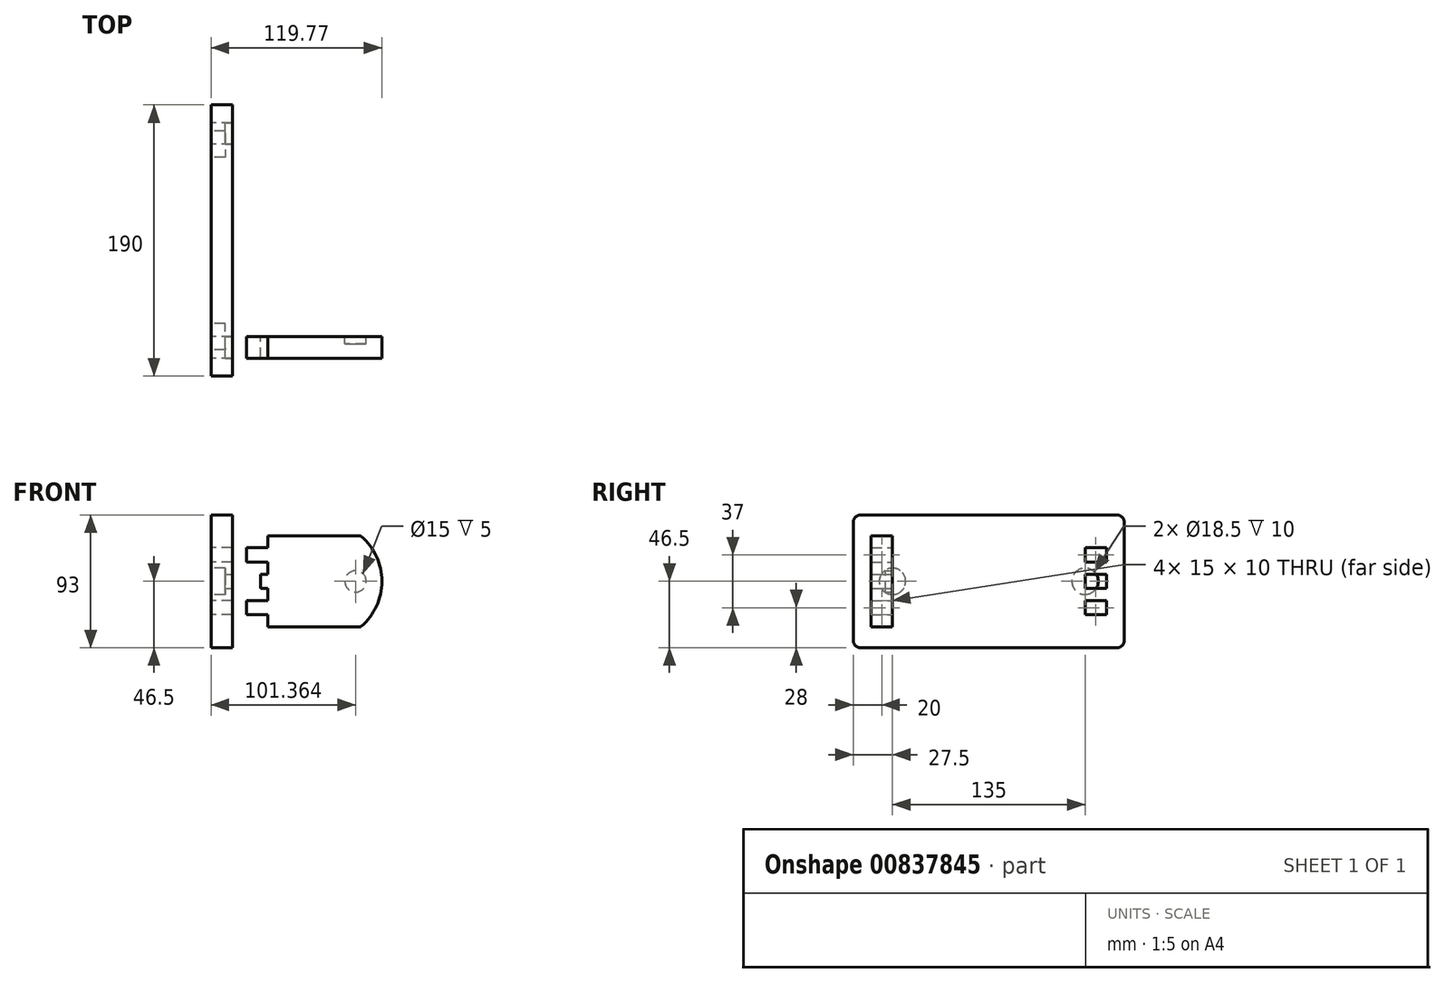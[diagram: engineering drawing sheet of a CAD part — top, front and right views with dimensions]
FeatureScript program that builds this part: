
annotation { "Feature Type Name" : "Feature", "Feature Type Description" : "" }
export const myFeature = defineFeature(function(context is Context, id is Id, definition is map)
    precondition{}
    {
        {
            var Q0;
            Q0=qCreatedBy(makeId("Right.planeOp"),FACE);
            var sketch = newSketch(context, id + "F0", { "sketchPlane" : qUnion([Q0])});
            skLineSegment(sketch, "E0.bottom", {"start": v(90, -46.5) * mm, "end": v(-90, -46.5) * mm});
            skLineSegment(sketch, "E0.top", {"start": v(90, 46.5) * mm, "end": v(-90, 46.5) * mm});
            skLineSegment(sketch, "E0.left", {"start": v(95, -41.5) * mm, "end": v(95, 41.5) * mm});
            skLineSegment(sketch, "E0.right", {"start": v(-95, -41.5) * mm, "end": v(-95, 41.5) * mm});
            skPoint(sketch, "E0.middle", {"position": v(0, 0) * mm});
            skLineSegment(sketch, "E1.bottom", {"start": v(67.5, 23.5) * mm, "end": v(82.5, 23.5) * mm});
            skLineSegment(sketch, "E1.top", {"start": v(67.5, 13.5) * mm, "end": v(82.5, 13.5) * mm});
            skLineSegment(sketch, "E1.left", {"start": v(67.5, 23.5) * mm, "end": v(67.5, 13.5) * mm});
            skLineSegment(sketch, "E1.right", {"start": v(82.5, 23.5) * mm, "end": v(82.5, 13.5) * mm});
            skLineSegment(sketch, "E2.bottom", {"start": v(67.5, -13.5) * mm, "end": v(82.5, -13.5) * mm});
            skLineSegment(sketch, "E2.top", {"start": v(67.5, -23.5) * mm, "end": v(82.5, -23.5) * mm});
            skLineSegment(sketch, "E2.left", {"start": v(67.5, -13.5) * mm, "end": v(67.5, -23.5) * mm});
            skLineSegment(sketch, "E2.right", {"start": v(82.5, -13.5) * mm, "end": v(82.5, -23.5) * mm});
            skLineSegment(sketch, "E3.bottom", {"start": v(-67.5, -13.5) * mm, "end": v(-82.5, -13.5) * mm});
            skLineSegment(sketch, "E3.top", {"start": v(-67.5, -23.5) * mm, "end": v(-82.5, -23.5) * mm});
            skLineSegment(sketch, "E3.left", {"start": v(-67.5, -13.5) * mm, "end": v(-67.5, -23.5) * mm});
            skLineSegment(sketch, "E3.right", {"start": v(-82.5, -13.5) * mm, "end": v(-82.5, -23.5) * mm});
            skLineSegment(sketch, "E4.bottom", {"start": v(-67.5, 13.5) * mm, "end": v(-82.5, 13.5) * mm});
            skLineSegment(sketch, "E4.top", {"start": v(-67.5, 23.5) * mm, "end": v(-82.5, 23.5) * mm});
            skLineSegment(sketch, "E4.left", {"start": v(-67.5, 13.5) * mm, "end": v(-67.5, 23.5) * mm});
            skLineSegment(sketch, "E4.right", {"start": v(-82.5, 13.5) * mm, "end": v(-82.5, 23.5) * mm});
            skPoint(sketch, "E5.visualSharp", {"position": v(-95, 46.5) * mm});
            skArc(sketch, "E5.filletArc", {"start": v(-90, 46.5) * mm, "mid": v(-93.54, 45.04) * mm, "end": v(-95, 41.5) * mm});
            skPoint(sketch, "E6.visualSharp", {"position": v(95, 46.5) * mm});
            skArc(sketch, "E6.filletArc", {"start": v(95, 41.5) * mm, "mid": v(93.54, 45.04) * mm, "end": v(90, 46.5) * mm});
            skPoint(sketch, "E7.visualSharp", {"position": v(95, -46.5) * mm});
            skArc(sketch, "E7.filletArc", {"start": v(90, -46.5) * mm, "mid": v(93.54, -45.04) * mm, "end": v(95, -41.5) * mm});
            skPoint(sketch, "E8.visualSharp", {"position": v(-95, -46.5) * mm});
            skArc(sketch, "E8.filletArc", {"start": v(-95, -41.5) * mm, "mid": v(-93.54, -45.04) * mm, "end": v(-90, -46.5) * mm});
            skCircle(sketch, "E9", {"center": v(-67.5, 0) * mm, "radius": 9.25 * mm});
            skCircle(sketch, "E10", {"center": v(67.5, 0) * mm, "radius": 9.25 * mm});
            skLineSegment(sketch, "E11.bottom", {"start": v(-67.5, 5) * mm, "end": v(-82.5, 5) * mm});
            skLineSegment(sketch, "E11.top", {"start": v(-67.5, -5) * mm, "end": v(-82.5, -5) * mm});
            skLineSegment(sketch, "E11.left", {"start": v(-67.5, 5) * mm, "end": v(-67.5, -5) * mm});
            skLineSegment(sketch, "E11.right", {"start": v(-82.5, 5) * mm, "end": v(-82.5, -5) * mm});
            skSolve(sketch);
        }
        {
            var Q0;
            Q0=makeQuery(id+"F0.imprint","IMPRINT",FACE,{"disambiguationData":[TD([[makeQuery(id+"F0.imprint","IMPRINT",EDGE,{"derivedFrom":sQuery(id+"F0.wireOp",EDGE,"E0.bottom")}),-1.0]])]});
            var Q1;
            {var subQ5=sQuery(id+"F0.wireOp",EDGE,"E1.left");var subQ6=sQuery(id+"F0.wireOp",EDGE,"E1.top");var subQ7=makeQuery(id+"F0.imprint","INTERSECT",VERTEX,{"derivedFrom":[subQ6,subQ5]});Q1=makeQuery(id+"F0.imprint","IMPRINT",FACE,{"disambiguationData":[TD([[makeQuery(id+"F0.imprint","IMPRINT",EDGE,{"disambiguationData":[TD([[subQ7,-1.0]])],"derivedFrom":subQ6}),-1.0]])]});}
            var Q2;
            {var subQ6=sQuery(id+"F0.wireOp",EDGE,"E3.bottom");var subQ8=sQuery(id+"F0.wireOp",EDGE,"E3.left");var subQ9=makeQuery(id+"F0.imprint","INTERSECT",VERTEX,{"derivedFrom":[subQ6,subQ8]});Q2=makeQuery(id+"F0.imprint","IMPRINT",FACE,{"disambiguationData":[TD([[makeQuery(id+"F0.imprint","IMPRINT",EDGE,{"disambiguationData":[TD([[subQ9,-1.0]])],"derivedFrom":subQ6}),-1.0]])]});}
            var Q3;
            Q3=makeQuery(id+"F0.imprint","IMPRINT",FACE,{"disambiguationData":[TD([[makeQuery(id+"F0.imprint","IMPRINT",EDGE,{"derivedFrom":sQuery(id+"F0.wireOp",EDGE,"E9")}),1.0]])]});
            var Q4;
            Q4=makeQuery(id+"F0.imprint","IMPRINT",FACE,{"disambiguationData":[TD([[makeQuery(id+"F0.imprint","IMPRINT",EDGE,{"derivedFrom":sQuery(id+"F0.wireOp",EDGE,"E10")}),1.0]])]});
            var Q5;
            {var subQ5=sQuery(id+"F0.wireOp",EDGE,"E11.right");Q5=makeQuery(id+"F0.imprint","IMPRINT",FACE,{"disambiguationData":[TD([[makeQuery(id+"F0.imprint","IMPRINT",EDGE,{"derivedFrom":subQ5}),1.0]])]});}
            extrude(context, id + "F1", {"entities" : qUnion([Q0, Q1, Q2, Q3, Q4, Q5]), "depth" : 15 * mm, "offsetDistance" : 25 * mm});
        }
        {
            var Q0;
            Q0=qCreatedBy(makeId("Front.planeOp"),FACE);
            cPlane(context, id + "F2", {"entities" : qUnion([Q0]), "cplaneType" : CPlaneType.OFFSET, "offset" : 67.5 * mm, "width" : 150 * mm, "height" : 150 * mm});
        }
        {
            var Q0;
            Q0=qCreatedBy(id+"F2.planeOp",FACE);
            var sketch = newSketch(context, id + "F3", { "sketchPlane" : qUnion([Q0])});
            skLineSegment(sketch, "E12", {"start": v(104.04, 32) * mm, "end": v(39.77, 32) * mm});
            skLineSegment(sketch, "E13", {"start": v(39.77, 32) * mm, "end": v(39.77, 23.5) * mm});
            skLineSegment(sketch, "E14", {"start": v(39.77, 23.5) * mm, "end": v(24.77, 23.5) * mm});
            skLineSegment(sketch, "E15", {"start": v(24.77, 23.5) * mm, "end": v(24.77, 13.5) * mm});
            skLineSegment(sketch, "E16", {"start": v(24.77, 13.5) * mm, "end": v(39.77, 13.5) * mm});
            skLineSegment(sketch, "E17", {"start": v(39.77, -13.5) * mm, "end": v(24.77, -13.5) * mm});
            skLineSegment(sketch, "E18", {"start": v(24.77, -13.5) * mm, "end": v(24.77, -23.5) * mm});
            skLineSegment(sketch, "E19", {"start": v(24.77, -23.5) * mm, "end": v(39.77, -23.5) * mm});
            skLineSegment(sketch, "E20", {"start": v(39.77, -23.5) * mm, "end": v(39.77, -32) * mm});
            skLineSegment(sketch, "E21", {"start": v(39.77, -32) * mm, "end": v(104.04, -32) * mm});
            skPoint(sketch, "E22", {"position": v(119.77, 0) * mm});
            skArc(sketch, "E23", {"start": v(105.35, -31.51) * mm, "mid": v(119.77, 0) * mm, "end": v(105.35, 31.51) * mm});
            skPoint(sketch, "E24.visualSharp", {"position": v(104.77, 32) * mm});
            skArc(sketch, "E24.filletArc", {"start": v(105.35, 31.51) * mm, "mid": v(104.74, 31.87) * mm, "end": v(104.04, 32) * mm});
            skPoint(sketch, "E25.visualSharp", {"position": v(104.77, -32) * mm});
            skArc(sketch, "E25.filletArc", {"start": v(104.04, -32) * mm, "mid": v(104.74, -31.87) * mm, "end": v(105.35, -31.51) * mm});
            skCircle(sketch, "E26", {"center": v(101.36, 0) * mm, "radius": 7.5 * mm});
            skLineSegment(sketch, "E27", {"start": v(39.77, 13.5) * mm, "end": v(39.77, 5) * mm});
            skLineSegment(sketch, "E28", {"start": v(39.77, 5) * mm, "end": v(34.77, 5) * mm});
            skLineSegment(sketch, "E29", {"start": v(34.77, 5) * mm, "end": v(34.77, -5) * mm});
            skLineSegment(sketch, "E30", {"start": v(34.77, -5) * mm, "end": v(39.77, -5) * mm});
            skLineSegment(sketch, "E31", {"start": v(39.77, -5) * mm, "end": v(39.77, -13.5) * mm});
            skLineSegment(sketch, "E32.bottom", {"start": v(53.14, 7.5) * mm, "end": v(63.14, 7.5) * mm});
            skLineSegment(sketch, "E32.top", {"start": v(53.14, -7.5) * mm, "end": v(63.14, -7.5) * mm});
            skLineSegment(sketch, "E32.left", {"start": v(53.14, 7.5) * mm, "end": v(53.14, -7.5) * mm});
            skLineSegment(sketch, "E32.right", {"start": v(63.14, 7.5) * mm, "end": v(63.14, -7.5) * mm});
            skLineSegment(sketch, "E33.bottom", {"start": v(101.36, 23.5) * mm, "end": v(86.36, 23.5) * mm});
            skLineSegment(sketch, "E33.top", {"start": v(101.36, 13.5) * mm, "end": v(86.36, 13.5) * mm});
            skLineSegment(sketch, "E33.left", {"start": v(101.36, 23.5) * mm, "end": v(101.36, 13.5) * mm});
            skLineSegment(sketch, "E33.right", {"start": v(86.36, 23.5) * mm, "end": v(86.36, 13.5) * mm});
            skLineSegment(sketch, "E34.bottom", {"start": v(101.36, -23.5) * mm, "end": v(86.36, -23.5) * mm});
            skLineSegment(sketch, "E34.top", {"start": v(101.36, -13.5) * mm, "end": v(86.36, -13.5) * mm});
            skLineSegment(sketch, "E34.left", {"start": v(101.36, -23.5) * mm, "end": v(101.36, -13.5) * mm});
            skLineSegment(sketch, "E34.right", {"start": v(86.36, -23.5) * mm, "end": v(86.36, -13.5) * mm});
            skSolve(sketch);
        }
        {
            var Q0;
            Q0=makeQuery(id+"F3.imprint","IMPRINT",FACE,{"disambiguationData":[TD([[makeQuery(id+"F3.imprint","IMPRINT",EDGE,{"derivedFrom":sQuery(id+"F3.wireOp",EDGE,"E12")}),1.0]])]});
            var Q1;
            Q1=makeQuery(id+"F3.imprint","IMPRINT",FACE,{"disambiguationData":[TD([[makeQuery(id+"F3.imprint","IMPRINT",EDGE,{"derivedFrom":sQuery(id+"F3.wireOp",EDGE,"E26")}),1.0]])]});
            var Q2;
            Q2=makeQuery(id+"F3.imprint","IMPRINT",FACE,{"disambiguationData":[TD([[makeQuery(id+"F3.imprint","IMPRINT",EDGE,{"derivedFrom":sQuery(id+"F3.wireOp",EDGE,"E33.bottom")}),1.0]])]});
            var Q3;
            Q3=makeQuery(id+"F3.imprint","IMPRINT",FACE,{"disambiguationData":[TD([[makeQuery(id+"F3.imprint","IMPRINT",EDGE,{"derivedFrom":sQuery(id+"F3.wireOp",EDGE,"E34.bottom")}),-1.0]])]});
            var Q4;
            Q4=makeQuery(id+"F3.imprint","IMPRINT",FACE,{"disambiguationData":[TD([[makeQuery(id+"F3.imprint","IMPRINT",EDGE,{"derivedFrom":sQuery(id+"F3.wireOp",EDGE,"E32.bottom")}),-1.0]])]});
            extrude(context, id + "F4", {"entities" : qUnion([Q0, Q1, Q2, Q3, Q4]), "depth" : 15 * mm, "offsetDistance" : 25 * mm});
        }
        {
            var Q0;
            Q0=makeQuery(id+"F3.imprint","IMPRINT",FACE,{"disambiguationData":[TD([[makeQuery(id+"F3.imprint","IMPRINT",EDGE,{"derivedFrom":sQuery(id+"F3.wireOp",EDGE,"E26")}),1.0]])]});
            extrude(context, id + "F5", {"entities" : qUnion([Q0]), "operationType" : NewBodyOperationType.REMOVE, "depth" : 5 * mm, "offsetDistance" : 25 * mm});
        }
        {
            var Q0;
            Q0=makeQuery(id+"F0.imprint","IMPRINT",FACE,{"disambiguationData":[TD([[makeQuery(id+"F0.imprint","IMPRINT",EDGE,{"derivedFrom":sQuery(id+"F0.wireOp",EDGE,"E10")}),1.0]])]});
            var Q1;
            Q1=makeQuery(id+"F0.imprint","IMPRINT",FACE,{"disambiguationData":[TD([[makeQuery(id+"F0.imprint","IMPRINT",EDGE,{"derivedFrom":sQuery(id+"F0.wireOp",EDGE,"E9")}),1.0]])]});
            extrude(context, id + "F6", {"entities" : qUnion([Q0, Q1]), "operationType" : NewBodyOperationType.REMOVE, "depth" : 10 * mm, "offsetDistance" : 25 * mm});
        }
        {
            var Q0;
            Q0=makeQuery(id+"F1.opExtrude","CAP_FACE",FACE,{"disambiguationData":[OSD([sQuery(id+"F0.wireOp",EDGE,"E0.bottom"),sQuery(id+"F0.wireOp",EDGE,"E0.top"),sQuery(id+"F0.wireOp",EDGE,"E0.left"),sQuery(id+"F0.wireOp",EDGE,"E0.right"),sQuery(id+"F0.wireOp",EDGE,"E1.bottom"),sQuery(id+"F0.wireOp",EDGE,"E1.top"),sQuery(id+"F0.wireOp",EDGE,"E1.left"),sQuery(id+"F0.wireOp",EDGE,"E1.right"),sQuery(id+"F0.wireOp",EDGE,"E2.bottom"),sQuery(id+"F0.wireOp",EDGE,"E2.top"),sQuery(id+"F0.wireOp",EDGE,"E2.left"),sQuery(id+"F0.wireOp",EDGE,"E2.right"),sQuery(id+"F0.wireOp",EDGE,"E3.bottom"),sQuery(id+"F0.wireOp",EDGE,"E3.top"),sQuery(id+"F0.wireOp",EDGE,"E3.left"),sQuery(id+"F0.wireOp",EDGE,"E3.right"),sQuery(id+"F0.wireOp",EDGE,"E4.bottom"),sQuery(id+"F0.wireOp",EDGE,"E4.top"),sQuery(id+"F0.wireOp",EDGE,"E4.left"),sQuery(id+"F0.wireOp",EDGE,"E4.right"),sQuery(id+"F0.wireOp",EDGE,"E5.filletArc"),sQuery(id+"F0.wireOp",EDGE,"E6.filletArc"),sQuery(id+"F0.wireOp",EDGE,"E7.filletArc"),sQuery(id+"F0.wireOp",EDGE,"E8.filletArc")])],"isStart":false});
            var sketch = newSketch(context, id + "F7", { "sketchPlane" : qUnion([Q0])});
            skLineSegment(sketch, "E35.bottom", {"start": v(-82.5, -5) * mm, "end": v(-67.5, -5) * mm});
            skLineSegment(sketch, "E35.top", {"start": v(-82.5, 5) * mm, "end": v(-67.5, 5) * mm});
            skLineSegment(sketch, "E35.left", {"start": v(-82.5, -5) * mm, "end": v(-82.5, 5) * mm});
            skLineSegment(sketch, "E35.right", {"start": v(-67.5, -5) * mm, "end": v(-67.5, 5) * mm});
            skPoint(sketch, "E35.middle", {"position": v(-75, 0) * mm});
            skLineSegment(sketch, "E36.bottom", {"start": v(67.5, -5) * mm, "end": v(82.5, -5) * mm});
            skLineSegment(sketch, "E36.top", {"start": v(67.5, 5) * mm, "end": v(82.5, 5) * mm});
            skLineSegment(sketch, "E36.left", {"start": v(67.5, -5) * mm, "end": v(67.5, 5) * mm});
            skLineSegment(sketch, "E36.right", {"start": v(82.5, -5) * mm, "end": v(82.5, 5) * mm});
            skPoint(sketch, "E36.middle", {"position": v(75, 0) * mm});
            skSolve(sketch);
        }
        {
            var Q0;
            Q0=makeQuery(id+"F7.imprint","IMPRINT",FACE,{"disambiguationData":[TD([[makeQuery(id+"F7.imprint","IMPRINT",EDGE,{"derivedFrom":sQuery(id+"F7.wireOp",EDGE,"E35.bottom")}),1.0]])]});
            var Q1;
            Q1=makeQuery(id+"F7.imprint","IMPRINT",FACE,{"disambiguationData":[TD([[makeQuery(id+"F7.imprint","IMPRINT",EDGE,{"derivedFrom":sQuery(id+"F7.wireOp",EDGE,"E36.bottom")}),1.0]])]});
            extrude(context, id + "F8", {"entities" : qUnion([Q0, Q1]), "operationType" : NewBodyOperationType.REMOVE, "oppositeDirection" : true, "depth" : 5 * mm, "offsetDistance" : 25 * mm});
        }
    });
